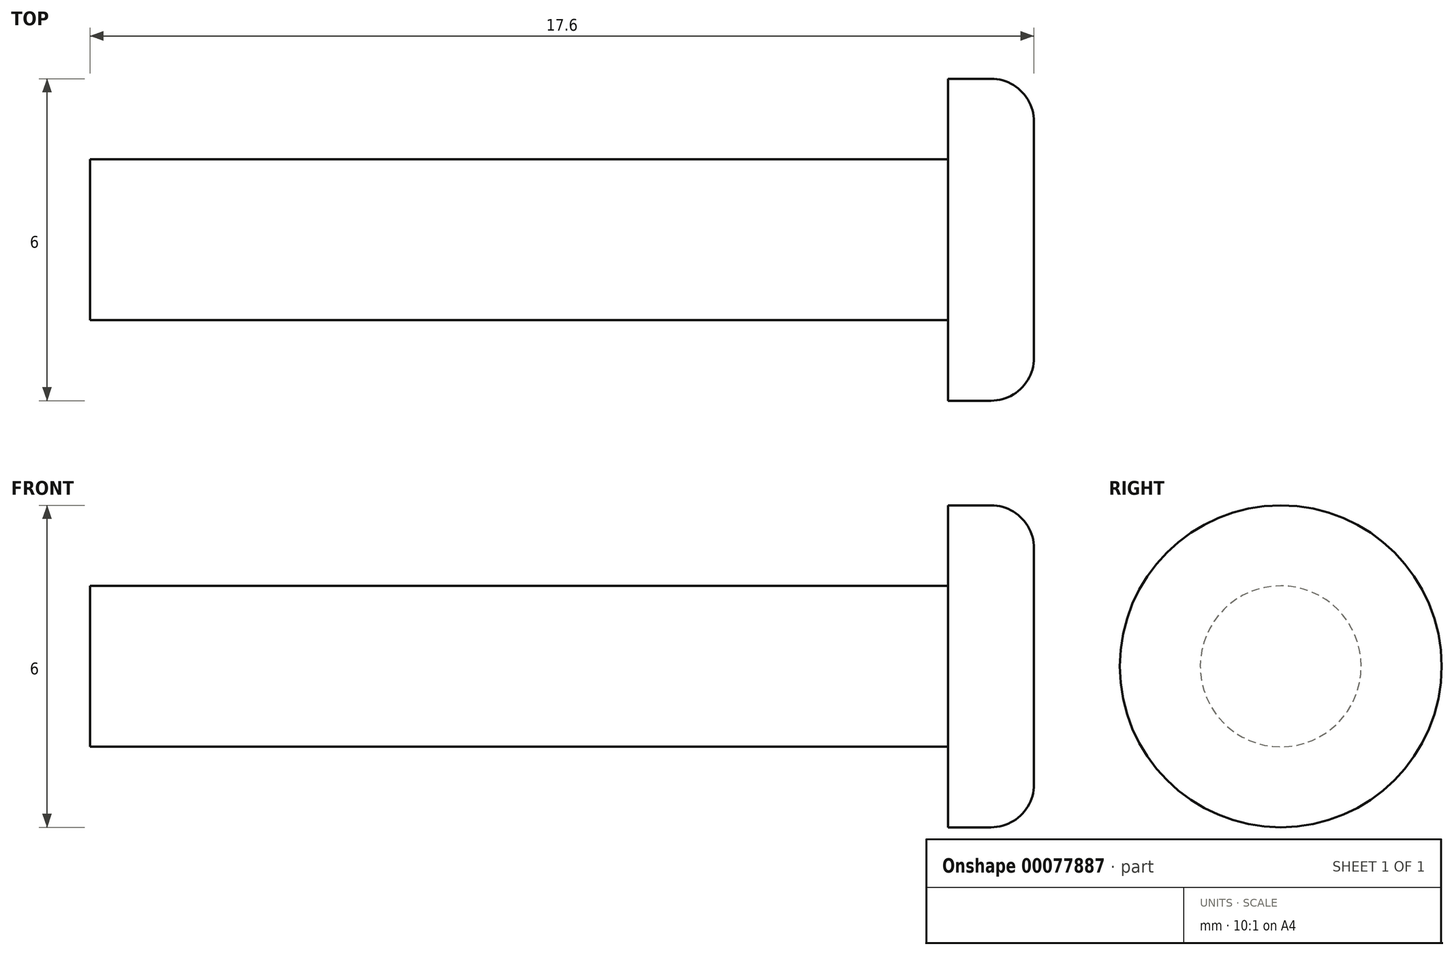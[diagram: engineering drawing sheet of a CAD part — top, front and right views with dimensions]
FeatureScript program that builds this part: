
annotation { "Feature Type Name" : "Feature", "Feature Type Description" : "" }
export const myFeature = defineFeature(function(context is Context, id is Id, definition is map)
    precondition{}
    {
        {
            var Q0;
            Q0=qCreatedBy(makeId("Front.planeOp"),FACE);
            var sketch = newSketch(context, id + "F0", { "sketchPlane" : qUnion([Q0])});
            skLineSegment(sketch, "E0", {"start": v(0, 0) * mm, "end": v(0, 1.5) * mm});
            skLineSegment(sketch, "E1", {"start": v(0, 1.5) * mm, "end": v(16, 1.5) * mm});
            skLineSegment(sketch, "E2", {"start": v(16, 1.5) * mm, "end": v(16, 3) * mm});
            skLineSegment(sketch, "E3", {"start": v(16, 3) * mm, "end": v(16.8, 3) * mm});
            skLineSegment(sketch, "E4", {"start": v(17.6, 2.2) * mm, "end": v(17.6, 0) * mm});
            skLineSegment(sketch, "E5", {"start": v(17.6, 0) * mm, "end": v(0, 0) * mm});
            skPoint(sketch, "E6.visualSharp", {"position": v(17.6, 3) * mm});
            skArc(sketch, "E6.filletArc", {"start": v(17.6, 2.2) * mm, "mid": v(17.37, 2.77) * mm, "end": v(16.8, 3) * mm});
            skSolve(sketch);
        }
        {
            var Q0;
            Q0=makeQuery(id+"F0.imprint","IMPRINT",FACE,{"disambiguationData":[TD([[makeQuery(id+"F0.imprint","IMPRINT",EDGE,{"derivedFrom":sQuery(id+"F0.wireOp",EDGE,"E0")}),-1.0]])]});
            var Q1;
            Q1=sQuery(id+"F0.wireOp",EDGE,"E5");
            revolve(context, id + "F1", {"entities" : qUnion([Q0]), "axis" : qUnion([Q1]), "revolveType" : RevolveType.FULL});
        }
    });
